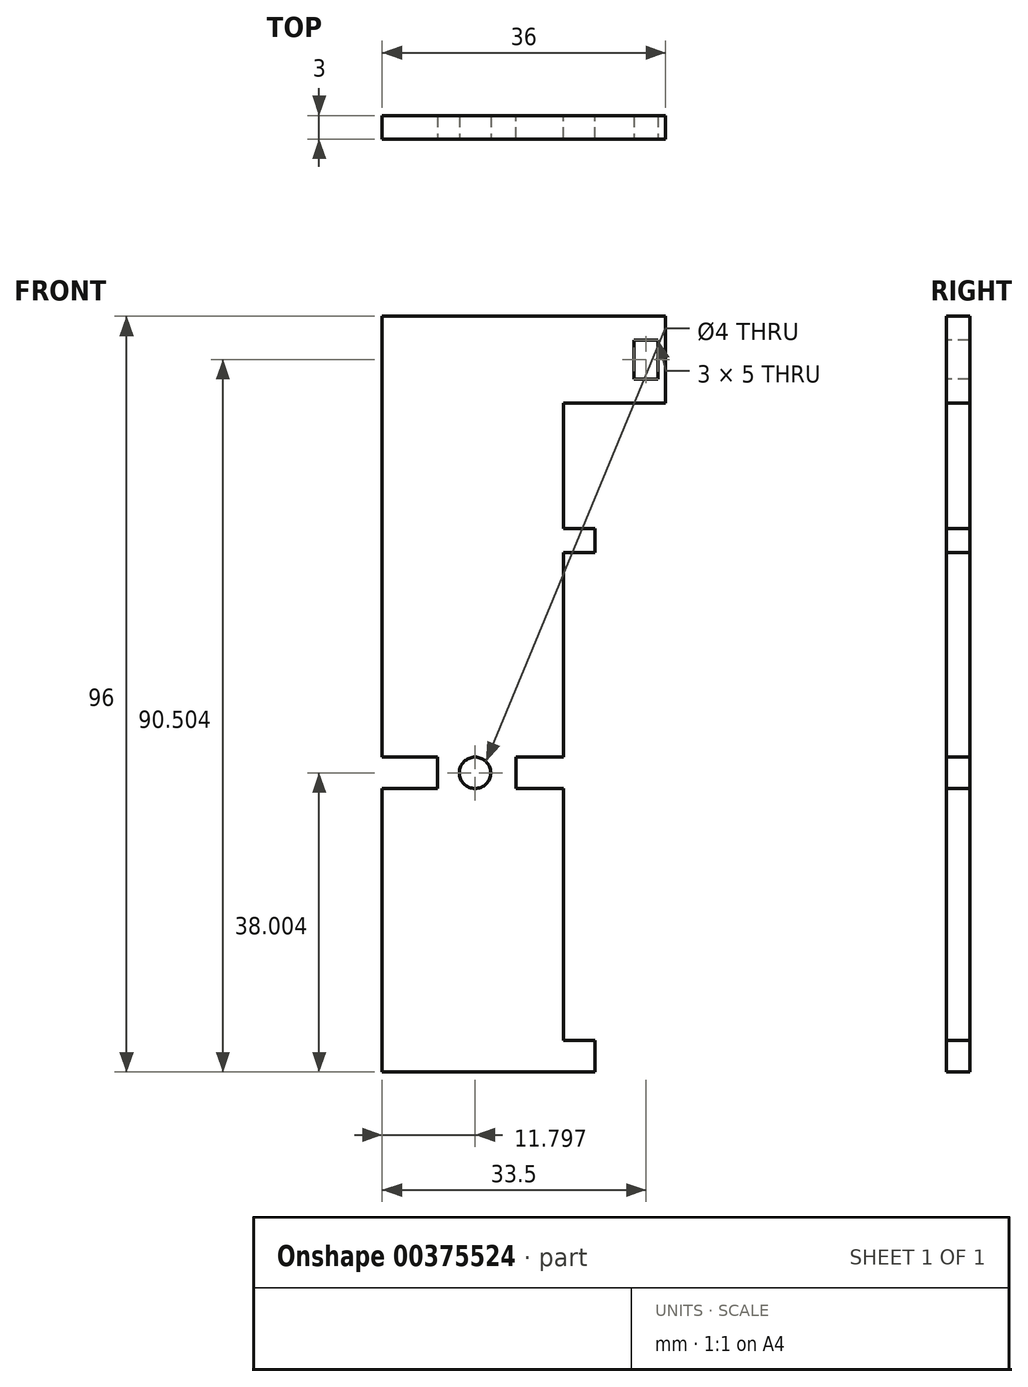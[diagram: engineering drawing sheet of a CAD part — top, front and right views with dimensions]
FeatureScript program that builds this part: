
annotation { "Feature Type Name" : "Feature", "Feature Type Description" : "" }
export const myFeature = defineFeature(function(context is Context, id is Id, definition is map)
    precondition{}
    {
        {
            var Q0;
            Q0=qCreatedBy(makeId("Front.planeOp"),FACE);
            var sketch = newSketch(context, id + "F0", { "sketchPlane" : qUnion([Q0])});
            skLineSegment(sketch, "E0.bottom", {"start": v(-15.03, 38.8) * mm, "end": v(20.97, 38.8) * mm});
            skLineSegment(sketch, "E0.top", {"start": v(-15.03, -57.2) * mm, "end": v(20.97, -57.2) * mm});
            skLineSegment(sketch, "E0.left", {"start": v(-15.03, 38.8) * mm, "end": v(-15.03, -57.2) * mm});
            skLineSegment(sketch, "E0.right", {"start": v(20.97, 38.8) * mm, "end": v(20.97, -57.2) * mm});
            skLineSegment(sketch, "E1", {"start": v(20.97, 38.8) * mm, "end": v(20.97, 27.8) * mm});
            skLineSegment(sketch, "E2", {"start": v(20.97, 27.8) * mm, "end": v(7.97, 27.8) * mm});
            skLineSegment(sketch, "E3", {"start": v(7.97, 27.8) * mm, "end": v(7.97, 11.8) * mm});
            skLineSegment(sketch, "E4", {"start": v(7.97, 11.8) * mm, "end": v(11.97, 11.8) * mm});
            skLineSegment(sketch, "E5", {"start": v(11.97, 11.8) * mm, "end": v(11.97, 8.8) * mm});
            skLineSegment(sketch, "E6", {"start": v(11.97, 8.8) * mm, "end": v(7.97, 8.8) * mm});
            skLineSegment(sketch, "E7", {"start": v(7.97, 8.8) * mm, "end": v(7.97, -17.2) * mm});
            skLineSegment(sketch, "E8", {"start": v(7.97, -17.2) * mm, "end": v(1.97, -17.2) * mm});
            skLineSegment(sketch, "E9", {"start": v(1.97, -17.2) * mm, "end": v(1.97, -21.2) * mm});
            skLineSegment(sketch, "E10", {"start": v(1.97, -21.2) * mm, "end": v(7.97, -21.2) * mm});
            skLineSegment(sketch, "E11", {"start": v(7.97, -53.2) * mm, "end": v(11.97, -53.2) * mm});
            skLineSegment(sketch, "E12", {"start": v(11.97, -53.2) * mm, "end": v(11.97, -57.2) * mm});
            skLineSegment(sketch, "E13", {"start": v(7.97, -53.2) * mm, "end": v(7.97, -21.2) * mm});
            skSolve(sketch);
        }
        {
            var Q0;
            Q0=makeQuery(id+"F0.imprint","IMPRINT",FACE,{"disambiguationData":[TD([[makeQuery(id+"F0.imprint","IMPRINT",EDGE,{"derivedFrom":sQuery(id+"F0.wireOp",EDGE,"E0.bottom")}),-1.0]])]});
            extrude(context, id + "F1", {"entities" : qUnion([Q0]), "depth" : 3 * mm});
        }
        {
            var Q0;
            Q0=makeQuery(id+"F1.opExtrude","CAP_FACE",FACE,{"disambiguationData":[OSD([sQuery(id+"F0.wireOp",EDGE,"E0.bottom"),sQuery(id+"F0.wireOp",EDGE,"E0.top"),sQuery(id+"F0.wireOp",EDGE,"E0.left"),sQuery(id+"F0.wireOp",EDGE,"E1"),sQuery(id+"F0.wireOp",EDGE,"E2"),sQuery(id+"F0.wireOp",EDGE,"E3"),sQuery(id+"F0.wireOp",EDGE,"E4"),sQuery(id+"F0.wireOp",EDGE,"E5"),sQuery(id+"F0.wireOp",EDGE,"E6"),sQuery(id+"F0.wireOp",EDGE,"E7"),sQuery(id+"F0.wireOp",EDGE,"E8"),sQuery(id+"F0.wireOp",EDGE,"E9"),sQuery(id+"F0.wireOp",EDGE,"E10"),sQuery(id+"F0.wireOp",EDGE,"E11"),sQuery(id+"F0.wireOp",EDGE,"E12"),sQuery(id+"F0.wireOp",EDGE,"E13")])],"isStart":false});
            var sketch = newSketch(context, id + "F2", { "sketchPlane" : qUnion([Q0])});
            skLineSegment(sketch, "E14", {"start": v(-15.03, -57.2) * mm, "end": v(-15.03, -21.2) * mm});
            skLineSegment(sketch, "E15", {"start": v(-15.03, -21.2) * mm, "end": v(-8.03, -21.2) * mm});
            skLineSegment(sketch, "E16", {"start": v(-8.03, -21.2) * mm, "end": v(-8.03, -17.2) * mm});
            skLineSegment(sketch, "E17", {"start": v(-8.03, -17.2) * mm, "end": v(-15.03, -17.2) * mm});
            skCircle(sketch, "E18", {"center": v(-3.23, -19.2) * mm, "radius": 2 * mm});
            skPoint(sketch, "E18.centerSnap0", {"position": v(1.97, -19.2) * mm});
            skLineSegment(sketch, "E19", {"start": v(20.97, 38.8) * mm, "end": v(19.97, 38.8) * mm});
            skLineSegment(sketch, "E20", {"start": v(19.97, 38.8) * mm, "end": v(19.97, 35.8) * mm});
            skLineSegment(sketch, "E21", {"start": v(19.97, 35.8) * mm, "end": v(16.97, 35.8) * mm});
            skLineSegment(sketch, "E22", {"start": v(16.97, 35.8) * mm, "end": v(16.97, 30.8) * mm});
            skLineSegment(sketch, "E23", {"start": v(16.97, 30.8) * mm, "end": v(19.97, 30.8) * mm});
            skLineSegment(sketch, "E24", {"start": v(19.97, 30.8) * mm, "end": v(19.97, 35.8) * mm});
            skSolve(sketch);
        }
        {
            var Q0;
            Q0=qSketchRegion(id+"F2",true);
            var Q1;
            {var subQ0=sQuery(id+"F2.wireOp",EDGE,"E15");Q1=makeQuery(id+"F2.imprint","IMPRINT",FACE,{"disambiguationData":[TD([[makeQuery(id+"F2.imprint","IMPRINT",EDGE,{"derivedFrom":subQ0}),1.0]])]});}
            extrude(context, id + "F3", {"entities" : qUnion([Q0, Q1]), "operationType" : NewBodyOperationType.REMOVE, "oppositeDirection" : true, "depth" : 25 * mm});
        }
    });
